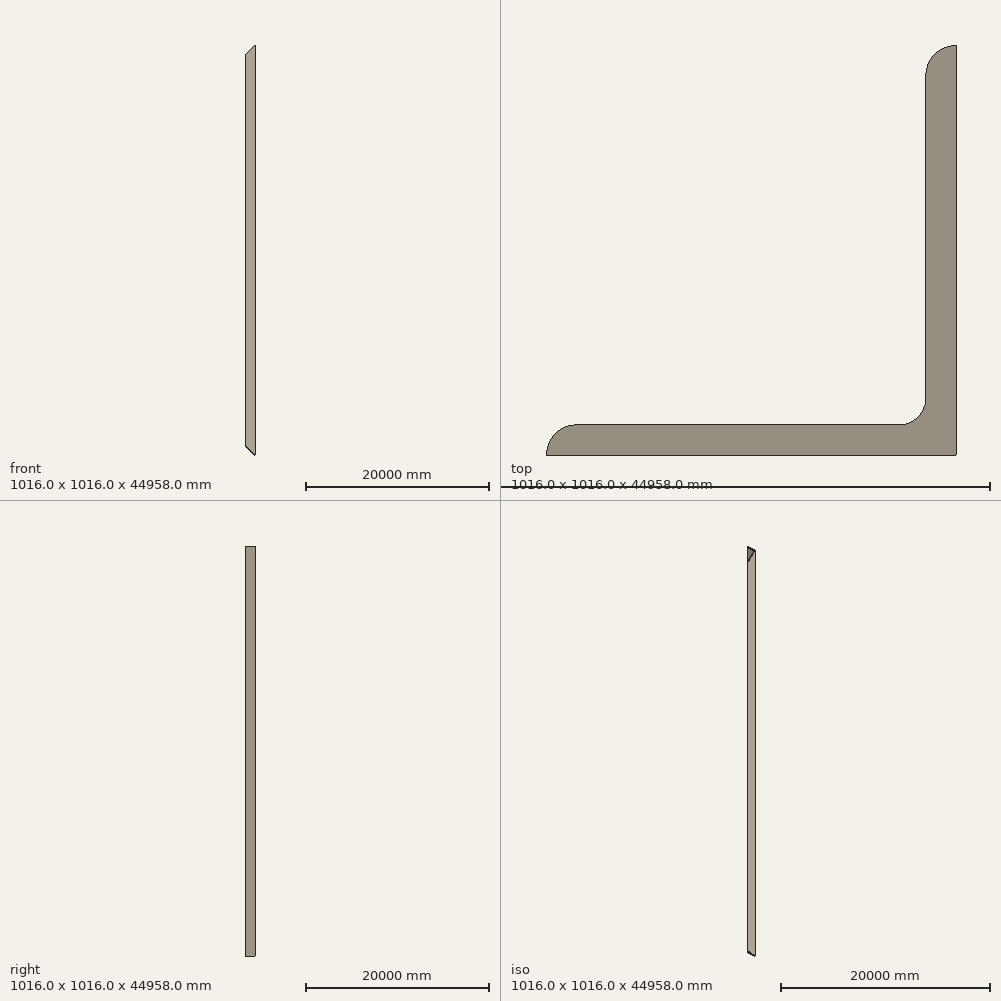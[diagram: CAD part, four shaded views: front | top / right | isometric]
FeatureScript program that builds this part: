
annotation { "Feature Type Name" : "Feature", "Feature Type Description" : "" }
export const myFeature = defineFeature(function(context is Context, id is Id, definition is map)
    precondition{}
    {
        {
            var Q0;
            Q0=qCreatedBy(makeId("Top.planeOp"),FACE);
            var sketch = newSketch(context, id + "F0", { "sketchPlane" : qUnion([Q0])});
            skLineSegment(sketch, "E0", {"start": v(0, 0) * mm, "end": v(1016, 0) * mm});
            skLineSegment(sketch, "E1", {"start": v(1016, 0) * mm, "end": v(1016, 1016) * mm});
            skLineSegment(sketch, "E2", {"start": v(939.8, 939.8) * mm, "end": v(939.8, 139.7) * mm});
            skLineSegment(sketch, "E3", {"start": v(876.3, 76.2) * mm, "end": v(76.2, 76.2) * mm});
            skArc(sketch, "E4", {"start": v(76.2, 76.2) * mm, "mid": v(22.32, 53.88) * mm, "end": v(0, 0) * mm});
            skArc(sketch, "E5", {"start": v(939.8, 939.8) * mm, "mid": v(962.12, 993.68) * mm, "end": v(1016, 1016) * mm});
            skPoint(sketch, "E6.visualSharp", {"position": v(939.8, 76.2) * mm});
            skArc(sketch, "E6.filletArc", {"start": v(876.3, 76.2) * mm, "mid": v(921.2, 94.8) * mm, "end": v(939.8, 139.7) * mm});
            skSolve(sketch);
        }
        {
            var Q0;
            Q0=makeQuery(id+"F0.imprint","IMPRINT",FACE,{"disambiguationData":[TD([[makeQuery(id+"F0.imprint","IMPRINT",EDGE,{"derivedFrom":sQuery(id+"F0.wireOp",EDGE,"E0")}),1.0]])]});
            var Q1;
            Q1 = qConstructionFilter(qBodyType(qCreatedBy(id + "F0" ,EDGE), BodyType.WIRE), ConstructionObject.NO);
            extrude(context, id + "F1", {"entities" : qUnion([Q0]), "surfaceEntities" : qUnion([Q1]), "depth" : 44958 * mm, "offsetDistance" : 25.4 * mm});
        }
        {
            var Q0;
            Q0=makeQuery(id+"F1.opExtrude","SWEPT_FACE",FACE,{"disambiguationData":[OSD([sQuery(id+"F0.wireOp",EDGE,"E0")])]});
            var sketch = newSketch(context, id + "F2", { "sketchPlane" : qUnion([Q0])});
            skLineSegment(sketch, "E7", {"start": v(1016, 44958) * mm, "end": v(-870.1, 43071.9) * mm});
            skLineSegment(sketch, "E8", {"start": v(-870.1, 43071.9) * mm, "end": v(-624.78, 48163.47) * mm});
            skLineSegment(sketch, "E9", {"start": v(-624.78, 48163.47) * mm, "end": v(1016, 44958) * mm});
            skLineSegment(sketch, "E10", {"start": v(1016, 0) * mm, "end": v(-514.86, 1530.86) * mm});
            skLineSegment(sketch, "E11", {"start": v(-514.86, 1530.86) * mm, "end": v(-8.34, -374.38) * mm});
            skLineSegment(sketch, "E12", {"start": v(-8.34, -374.38) * mm, "end": v(1016, 0) * mm});
            skSolve(sketch);
        }
        {
            var Q0;
            {var subQ1=sQuery(id+"F0.wireOp",EDGE,"E0");var subQ2=makeQuery(id+"F1.opExtrude","CAP_EDGE",EDGE,{"disambiguationData":[OSD([subQ1])],"isStart":true});Q0=makeQuery(id+"F2.imprint","IMPRINT",FACE,{"disambiguationData":[TD([[makeQuery(id+"F2.imprint","IMPRINT",EDGE,{"derivedFrom":subQ2}),1.0]])]});}
            var Q1;
            {var subQ1=sQuery(id+"F0.wireOp",EDGE,"E0");var subQ2=makeQuery(id+"F1.opExtrude","CAP_EDGE",EDGE,{"disambiguationData":[OSD([subQ1])],"isStart":false});Q1=makeQuery(id+"F2.imprint","IMPRINT",FACE,{"disambiguationData":[TD([[makeQuery(id+"F2.imprint","IMPRINT",EDGE,{"derivedFrom":subQ2}),-1.0]])]});}
            extrude(context, id + "F3", {"entities" : qUnion([Q0, Q1]), "operationType" : NewBodyOperationType.REMOVE, "endBound" : BoundingType.THROUGH_ALL, "oppositeDirection" : true, "depth" : 25.4 * mm, "offsetDistance" : 25.4 * mm});
        }
    });
